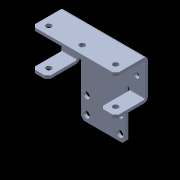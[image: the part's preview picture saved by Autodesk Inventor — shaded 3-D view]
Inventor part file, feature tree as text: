
AUTODESK INVENTOR PART (.ipt)
format: ipt  version: 2016 (Build 200138000, 138)  size: 161,792 bytes
history: native  units: in
note: dims shown in document units (in); Inventor stores cm internally (conversion verified against a paired STEP export)
features: chamfer x1, other x1, imported_body x1
ambient origin geometry x8: Origin, YZ Plane, XZ Plane, XY Plane, X Axis, Y Axis, Z Axis, Center Point
bodies: Body1 (feature_tree)
feature tree (3):
  chamfer  "Chamfer1"  [1 undecoded]
  other  "VersaFrame VersaPlanetary Side Mount1"
  imported_body  "Base1"
note: 1 required parameter value undecoded (feature->parameter linkage not recoverable at this tier; creation-order binding heuristic only, values carry confidence <= 0.55)
